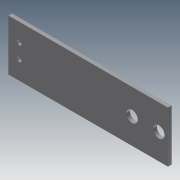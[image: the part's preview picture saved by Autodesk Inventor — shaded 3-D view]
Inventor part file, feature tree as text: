
AUTODESK INVENTOR PART (.ipt)
format: ipt  version: 2011 (Build 150239000, 239)  size: 112,128 bytes
history: native  units: in
note: dims shown in document units (in); Inventor stores cm internally (conversion verified against a paired STEP export)
features: extrude x6, sketch x6
ambient origin geometry x8: Origin, YZ Plane, XZ Plane, XY Plane, X Axis, Y Axis, Z Axis, Center Point
bodies: Solid1 (feature_tree)
feature tree (12):
  extrude  "Extrusion1"  Depth=1.26in
  extrude  "Extrusion2"  Depth=0.5in TaperAngle=0.0deg
  extrude  "Extrusion3"  Depth=0.25in
  extrude  "Extrusion4"  Depth=0.156in
  extrude  "Extrusion5"  Depth=0.315in
  extrude  "Extrusion6"  Depth=0.5in TaperAngle=0.0deg
  sketch  "Sketch1"  dims[d0=5.5in d1=1.26in]
  sketch  "Sketch2"  dims[d2=0.125in d3=0.0in d4=0.5in d5=0.0in]
  sketch  "Sketch3"  dims[d6=0.75in d7=0.25in]
  sketch  "Sketch4"  dims[d8=0.25in d9=0.156in]
  sketch  "Sketch5"  dims[d10=0.5in d11=0.0in d12=0.315in]
  sketch  "Sketch6"  dims[d13=0.394in d14=0.5in d15=0.0in d16=0.125in d17=0.0in d18=0.315in d19=0.3937in d20=1.1811in d21=0.125in d22=0.0in]
